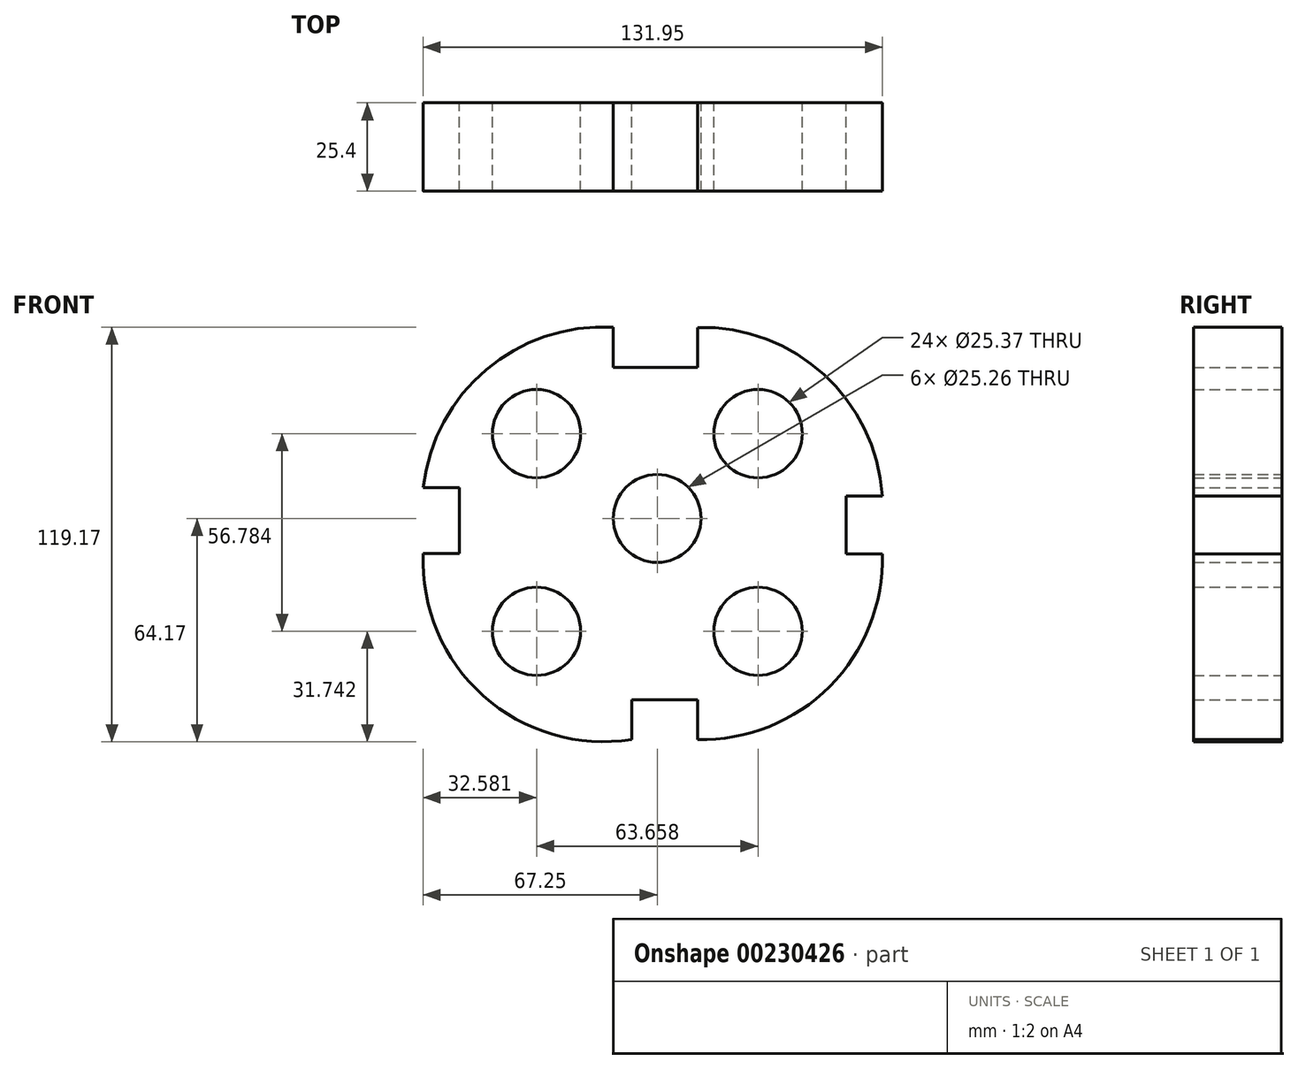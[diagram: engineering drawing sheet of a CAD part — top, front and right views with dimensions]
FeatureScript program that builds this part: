
annotation { "Feature Type Name" : "Feature", "Feature Type Description" : "" }
export const myFeature = defineFeature(function(context is Context, id is Id, definition is map)
    precondition{}
    {
        {
            var Q0;
            Q0=qCreatedBy(makeId("Front.planeOp"),FACE);
            var sketch = newSketch(context, id + "F0", { "sketchPlane" : qUnion([Q0])});
            skLineSegment(sketch, "E0", {"start": v(54.3, 6.4) * mm, "end": v(54.3, -10.22) * mm});
            skLineSegment(sketch, "E1", {"start": v(-56.82, 8.82) * mm, "end": v(-56.82, -10.09) * mm});
            skLineSegment(sketch, "E2", {"start": v(-56.82, 8.82) * mm, "end": v(-67.2, 8.82) * mm});
            skLineSegment(sketch, "E3", {"start": v(-56.82, -10.09) * mm, "end": v(-67.2, -10.09) * mm});
            skLineSegment(sketch, "E4", {"start": v(54.3, 6.4) * mm, "end": v(64.68, 6.4) * mm});
            skLineSegment(sketch, "E5", {"start": v(54.3, -10.22) * mm, "end": v(64.68, -10.22) * mm});
            skLineSegment(sketch, "E6", {"start": v(-12.65, 43.45) * mm, "end": v(11.58, 43.45) * mm});
            skLineSegment(sketch, "E7", {"start": v(-7.32, -52.07) * mm, "end": v(11.58, -52.07) * mm});
            skLineSegment(sketch, "E8", {"start": v(-12.65, 43.45) * mm, "end": v(-12.65, 54.91) * mm});
            skLineSegment(sketch, "E9", {"start": v(11.58, 54.87) * mm, "end": v(11.58, 43.45) * mm});
            skLineSegment(sketch, "E10", {"start": v(-7.32, -52.07) * mm, "end": v(-7.32, -63.53) * mm});
            skLineSegment(sketch, "E11", {"start": v(11.58, -52.07) * mm, "end": v(11.58, -63.53) * mm});
            skArc(sketch, "E12", {"start": v(-12.65, 54.91) * mm, "mid": v(-49.13, 42.75) * mm, "end": v(-67.2, 8.82) * mm});
            skArc(sketch, "E13", {"start": v(-67.2, -10.09) * mm, "mid": v(-49.93, -51) * mm, "end": v(-7.32, -63.53) * mm});
            skArc(sketch, "E14", {"start": v(11.58, -63.53) * mm, "mid": v(49.59, -48.28) * mm, "end": v(64.68, -10.22) * mm});
            skArc(sketch, "E15", {"start": v(64.68, 6.4) * mm, "mid": v(47.9, 41.33) * mm, "end": v(11.58, 54.87) * mm});
            skCircle(sketch, "E16", {"center": v(0, 0) * mm, "radius": 12.63 * mm});
            skCircle(sketch, "E17", {"center": v(28.99, 24.36) * mm, "radius": 12.68 * mm});
            skCircle(sketch, "E18", {"center": v(-34.67, 24.36) * mm, "radius": 12.68 * mm});
            skCircle(sketch, "E19", {"center": v(-34.67, -32.43) * mm, "radius": 12.68 * mm});
            skCircle(sketch, "E20", {"center": v(28.99, -32.43) * mm, "radius": 12.68 * mm});
            skSolve(sketch);
        }
        {
            var Q0;
            Q0 = qSketchRegion(id + "F0", true);
            extrude(context, id + "F1", {"entities" : qUnion([Q0]), "depth" : 25.4 * mm});
        }
    });
